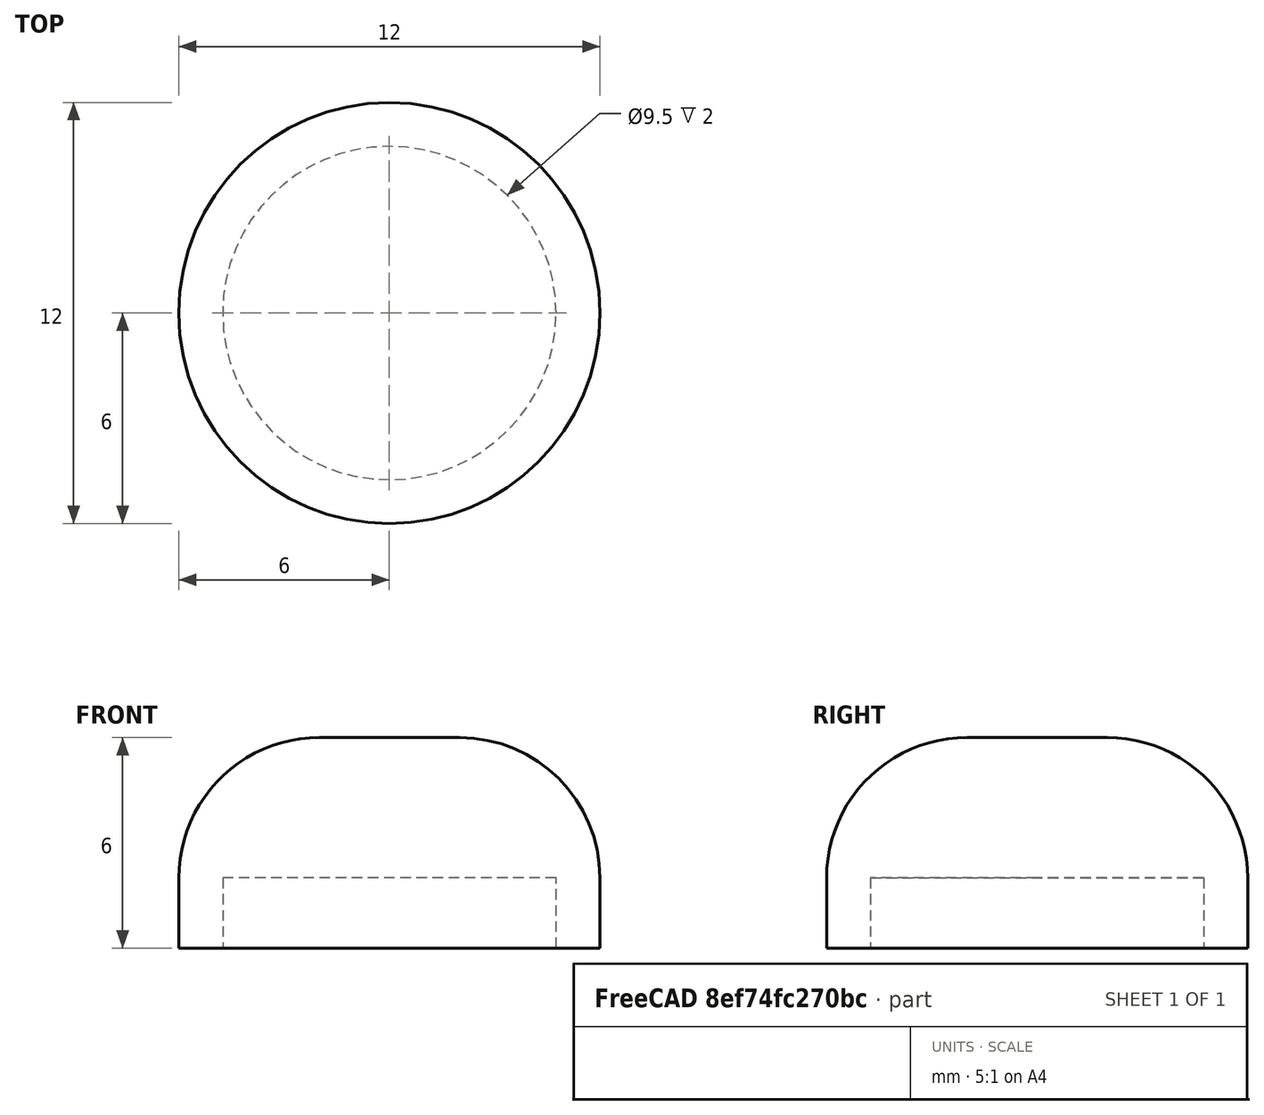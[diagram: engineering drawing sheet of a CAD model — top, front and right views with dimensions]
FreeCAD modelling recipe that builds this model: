
FCSTD DOCUMENT  (FreeCAD 0.18R4 (GitTag))
Label: keyboardSWPart4
License: All rights reserved
LicenseURL: http://en.wikipedia.org/wiki/All_rights_reserved
objects: Mesh::Feature×4, Sketcher::SketchObject×2, PartDesign::Pad×1, PartDesign::Fillet×1, PartDesign::Pocket×1, PartDesign::Body×1
note: 8 computed .brp shape members not serialized (recipe doc carries the construction recipe); baked Part::Feature solids carry a one-line shape summary decoded from their .brp

FEATURE [Sketcher::SketchObject] Sketch
  MapMode = 5
  Support = -> [XY_Plane]
  sketch-geometry (1):
    g0: Circle CenterX=0 CenterY=0 CenterZ=0 NormalX=0 NormalY=0 NormalZ=1 AngleXU=0 Radius=6
  constraints (2):
    c: Coincident(g0,g-1)
    c: Radius(g0) = 6
FEATURE [PartDesign::Pad] Pad
  Length = 6
  Length2 = 100
  Profile = -> Sketch
  Type = 0
FEATURE [PartDesign::Fillet] Fillet
  Base = -> Pad [Edge3]
  BaseFeature = -> Pad
  Radius = 4
FEATURE [Sketcher::SketchObject] Sketch001
  MapMode = 5
  Placement = pos=(0,0,0) rot=(1,0,0;3.14159rad)
  Support = -> [Fillet]
  sketch-geometry (1):
    g0: Circle CenterX=0 CenterY=0 CenterZ=0 NormalX=0 NormalY=0 NormalZ=1 AngleXU=0 Radius=4.75
  constraints (2):
    c: Coincident(g0,g-1)
    c: Radius(g0) = 4.75
FEATURE [PartDesign::Pocket] Pocket
  BaseFeature = -> Fillet
  Length = 2
  Length2 = 100
  Profile = -> Sketch001
  Type = 0
FEATURE [PartDesign::Body] Body
  Group = -> [Sketch,Pad,Fillet,Sketch001,Pocket]
  Origin = -> Origin
  Tip = -> Pocket
FEATURE [Mesh::Feature] Mesh  label="Body (Meshed)"
FEATURE [Mesh::Feature] Mesh001  label="Pad (Meshed)"
FEATURE [Mesh::Feature] Mesh002  label="Fillet (Meshed)"
FEATURE [Mesh::Feature] Mesh003  label="Pocket (Meshed)"
